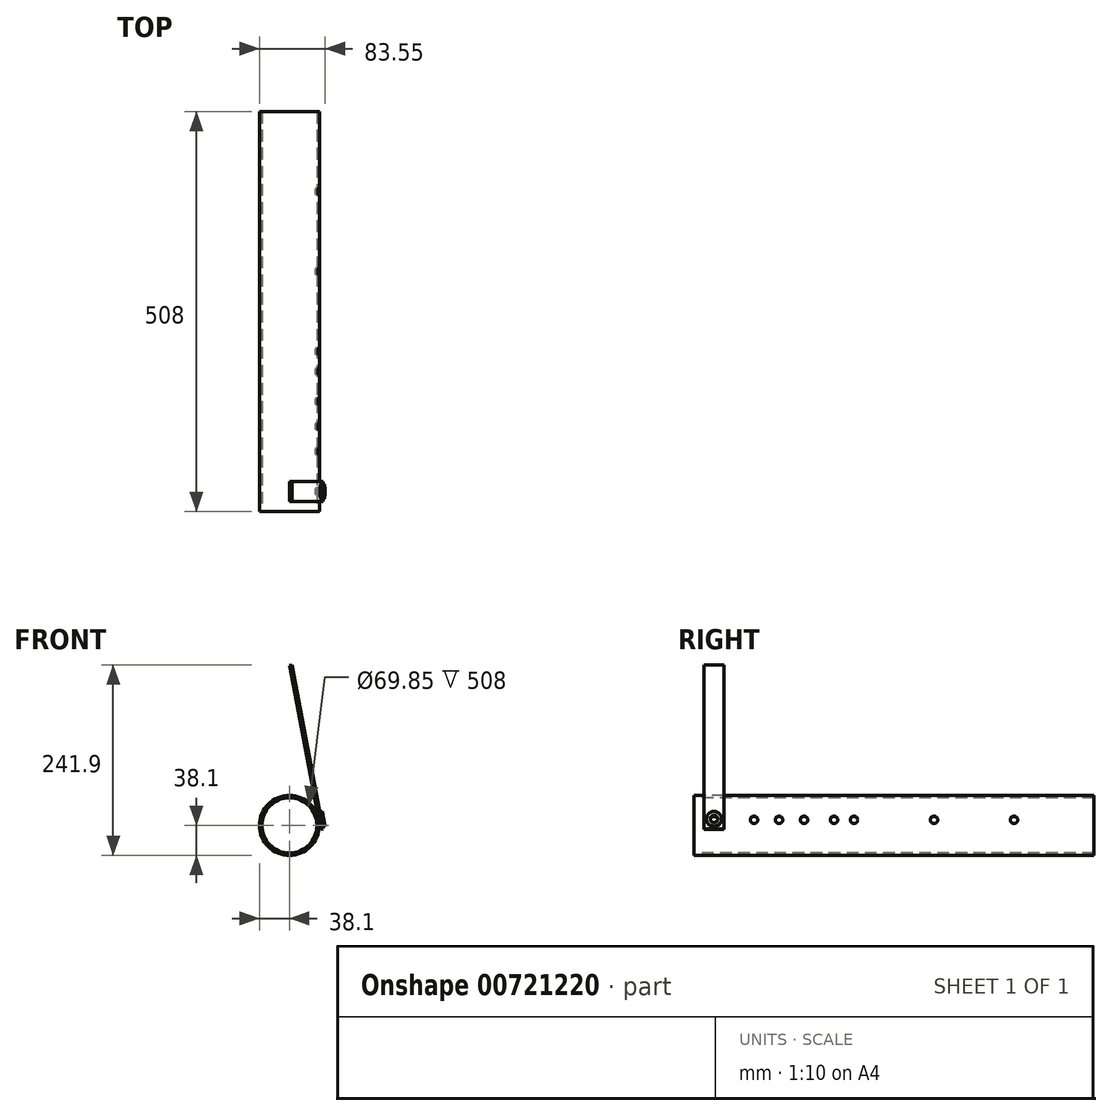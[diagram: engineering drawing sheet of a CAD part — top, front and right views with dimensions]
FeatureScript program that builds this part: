
annotation { "Feature Type Name" : "Feature", "Feature Type Description" : "" }
export const myFeature = defineFeature(function(context is Context, id is Id, definition is map)
    precondition{}
    {
        {
            var Q0;
            Q0=qCreatedBy(makeId("Front.planeOp"),FACE);
            var sketch = newSketch(context, id + "F0", { "sketchPlane" : qUnion([Q0])});
            skCircle(sketch, "E0", {"center": v(0, 0) * mm, "radius": 38.1 * mm});
            skCircle(sketch, "E1", {"center": v(0, 0) * mm, "radius": 34.93 * mm});
            skSolve(sketch);
        }
        {
            var Q0;
            Q0 = qSketchRegion(id + "F0", true);
            extrude(context, id + "F1", {"entities" : qUnion([Q0]), "oppositeDirection" : true, "depth" : 508 * mm, "offsetDistance" : 25.4 * mm});
        }
        {
            var Q0;
            Q0=qCreatedBy(makeId("Front.planeOp"),FACE);
            cPlane(context, id + "F2", {"entities" : qUnion([Q0]), "cplaneType" : CPlaneType.OFFSET, "offset" : 25.4 * mm, "oppositeDirection" : true, "width" : 152.4 * mm, "height" : 152.4 * mm});
        }
        {
            var Q0;
            Q0=qCreatedBy(id+"F2.planeOp",FACE);
            var sketch = newSketch(context, id + "F3", { "sketchPlane" : qUnion([Q0])});
            skLineSegment(sketch, "E2", {"start": v(0, 203.2) * mm, "end": v(39.8, -5.33) * mm});
            skLineSegment(sketch, "E3", {"start": v(39.8, -5.33) * mm, "end": v(42.92, -4.74) * mm});
            skLineSegment(sketch, "E4", {"start": v(42.92, -4.74) * mm, "end": v(3.12, 203.8) * mm});
            skLineSegment(sketch, "E5", {"start": v(3.12, 203.8) * mm, "end": v(0, 203.2) * mm});
            skLineSegment(sketch, "E6", {"start": v(0, 0) * mm, "end": v(0, 203.2) * mm, "construction": true});
            skLineSegment(sketch, "E7.MirrorCS", {"start": v(0, 203.2) * mm, "end": v(-39.8, -5.33) * mm, "construction": true});
            skLineSegment(sketch, "E8", {"start": v(0, 0) * mm, "end": v(40.54, 7.74) * mm, "construction": true});
            skSolve(sketch);
        }
        {
            var Q0;
            Q0 = qSketchRegion(id + "F3", true);
            extrude(context, id + "F4", {"entities" : qUnion([Q0]), "operationType" : NewBodyOperationType.ADD, "depth" : 25.4 * mm, "offsetDistance" : 25.4 * mm, "symmetric" : true});
        }
        {
            var Q0;
            Q0=makeQuery(id+"F4.opExtrude","SWEPT_FACE",FACE,{"disambiguationData":[OSD([sQuery(id+"F3.wireOp",EDGE,"E2")])]});
            var sketch = newSketch(context, id + "F5", { "sketchPlane" : qUnion([Q0])});
            skCircle(sketch, "E9", {"center": v(-25.4, 0) * mm, "radius": 4.76 * mm});
            skLineSegment(sketch, "E10", {"start": v(-25.4, 0) * mm, "end": v(-486.37, 0) * mm, "construction": true});
            skCircle(sketch, "E11", {"center": v(-139.7, 0) * mm, "radius": 4.76 * mm});
            skCircle(sketch, "E12", {"center": v(-177.8, 0) * mm, "radius": 4.76 * mm});
            skCircle(sketch, "E13", {"center": v(-304.8, 0) * mm, "radius": 4.76 * mm});
            skCircle(sketch, "E14", {"center": v(-406.4, 0) * mm, "radius": 4.76 * mm});
            skCircle(sketch, "E15", {"center": v(-76.2, 0) * mm, "radius": 4.76 * mm});
            skCircle(sketch, "E16", {"center": v(-203.2, 0) * mm, "radius": 4.76 * mm});
            skCircle(sketch, "E17", {"center": v(-107.95, 0) * mm, "radius": 4.76 * mm});
            skSolve(sketch);
        }
        {
            var Q0;
            Q0 = qSketchRegion(id + "F5", true);
            var Q1;
            Q1=qCreatedBy(makeId("Origin.pointOp"),VERTEX);
            extrude(context, id + "F6", {"entities" : qUnion([Q0]), "operationType" : NewBodyOperationType.REMOVE, "endBound" : BoundingType.UP_TO_VERTEX, "depth" : 25.4 * mm, "endBoundEntityVertex" : qUnion([Q1]), "offsetDistance" : 25.4 * mm, "hasSecondDirection" : true, "secondDirectionBound" : BoundingType.THROUGH_ALL, "secondDirectionOppositeDirection" : true, "secondDirectionDepth" : 25.4 * mm});
        }
        {
            var Q0;
            Q0=makeQuery(id+"F4.opExtrude","SWEPT_FACE",FACE,{"disambiguationData":[OSD([sQuery(id+"F3.wireOp",EDGE,"E4")])]});
            var sketch = newSketch(context, id + "F7", { "sketchPlane" : qUnion([Q0])});
            skCircle(sketch, "E18", {"center": v(25.4, 0) * mm, "radius": 9.53 * mm});
            skCircle(sketch, "E19.0", {"center": v(25.4, 0) * mm, "radius": 4.76 * mm});
            skSolve(sketch);
        }
        {
            var Q0;
            Q0 = qSketchRegion(id + "F7", true);
            extrude(context, id + "F8", {"entities" : qUnion([Q0]), "depth" : 3.17 * mm, "offsetDistance" : 25.4 * mm});
        }
    });
